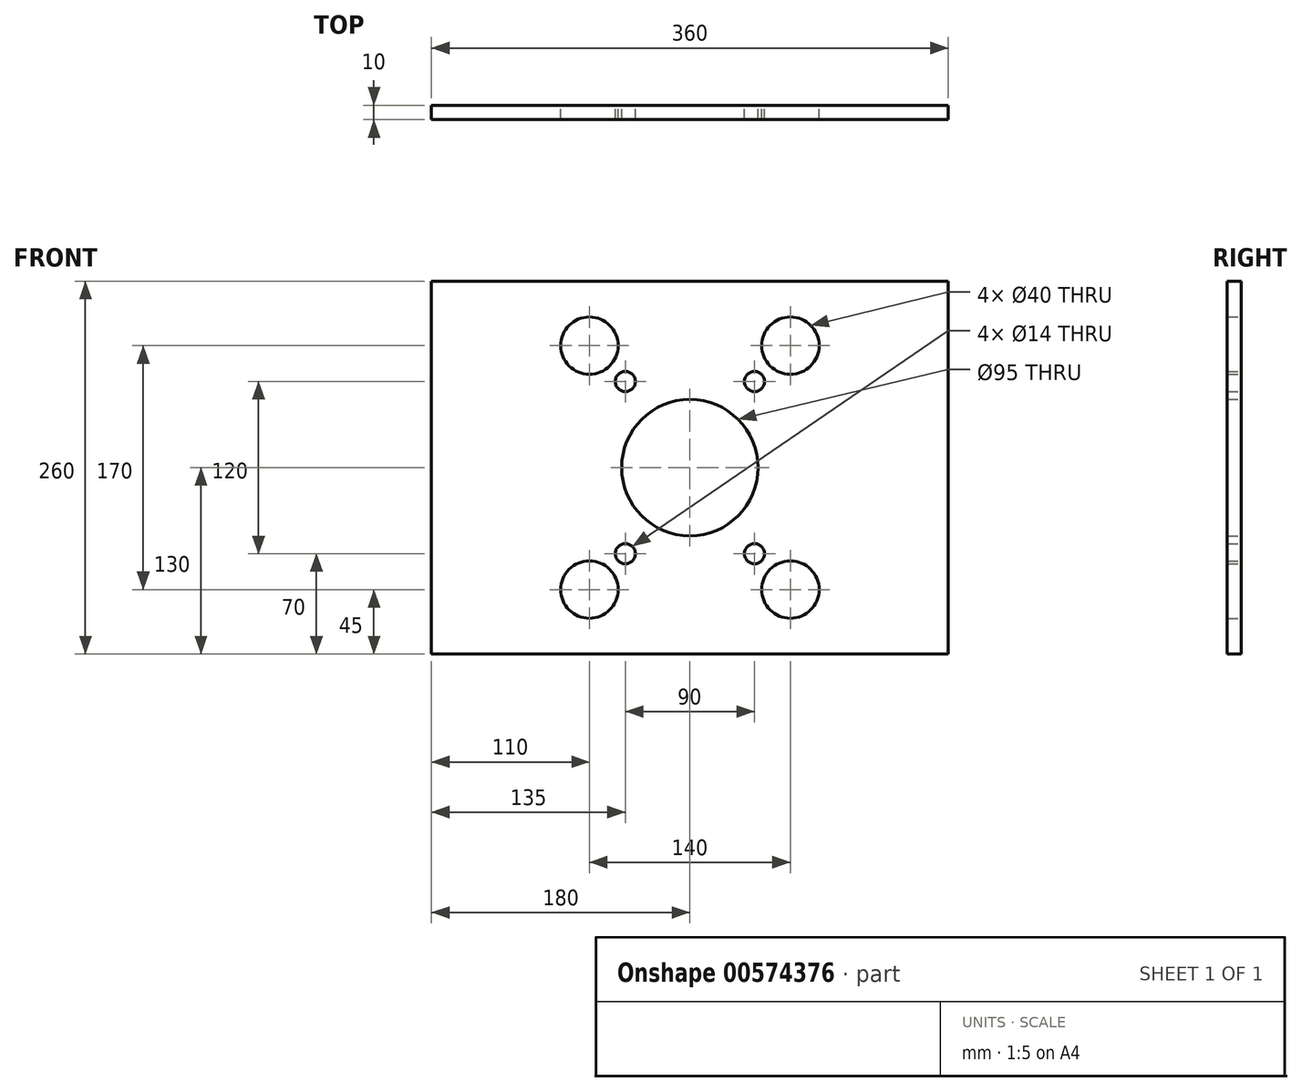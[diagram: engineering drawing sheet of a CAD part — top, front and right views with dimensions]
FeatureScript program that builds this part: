
annotation { "Feature Type Name" : "Feature", "Feature Type Description" : "" }
export const myFeature = defineFeature(function(context is Context, id is Id, definition is map)
    precondition{}
    {
        {
            var Q0;
            Q0=qCreatedBy(makeId("Front.planeOp"),FACE);
            var sketch = newSketch(context, id + "F0", { "sketchPlane" : qUnion([Q0])});
            skLineSegment(sketch, "E0.bottom", {"start": v(-180, 130) * mm, "end": v(180, 130) * mm});
            skLineSegment(sketch, "E0.top", {"start": v(-180, -130) * mm, "end": v(180, -130) * mm});
            skLineSegment(sketch, "E0.left", {"start": v(-180, 130) * mm, "end": v(-180, -130) * mm});
            skLineSegment(sketch, "E0.right", {"start": v(180, 130) * mm, "end": v(180, -130) * mm});
            skLineSegment(sketch, "E1", {"start": v(-180, 85) * mm, "end": v(180, 85) * mm, "construction": true});
            skLineSegment(sketch, "E2", {"start": v(-180, -85) * mm, "end": v(180, -85) * mm, "construction": true});
            skCircle(sketch, "E3", {"center": v(-70, 85) * mm, "radius": 20 * mm});
            skCircle(sketch, "E4", {"center": v(70, 85) * mm, "radius": 20 * mm});
            skCircle(sketch, "E5", {"center": v(-70, -85) * mm, "radius": 20 * mm});
            skCircle(sketch, "E6", {"center": v(70, -85) * mm, "radius": 20 * mm});
            skLineSegment(sketch, "E7", {"start": v(-180, 60) * mm, "end": v(180, 60) * mm, "construction": true});
            skLineSegment(sketch, "E8", {"start": v(-180, -60) * mm, "end": v(180, -60) * mm, "construction": true});
            skCircle(sketch, "E9", {"center": v(0, 0) * mm, "radius": 47.5 * mm});
            skCircle(sketch, "E10", {"center": v(-45, 60) * mm, "radius": 7 * mm});
            skCircle(sketch, "E11", {"center": v(-45, -60) * mm, "radius": 7 * mm});
            skCircle(sketch, "E12", {"center": v(45, 60) * mm, "radius": 7 * mm});
            skCircle(sketch, "E13", {"center": v(45, -60) * mm, "radius": 7 * mm});
            skSolve(sketch);
        }
        {
            var Q0;
            Q0=makeQuery(id+"F0.imprint","IMPRINT",FACE,{"disambiguationData":[TD([[makeQuery(id+"F0.imprint","IMPRINT",EDGE,{"derivedFrom":sQuery(id+"F0.wireOp",EDGE,"E0.bottom")}),-1.0]])]});
            extrude(context, id + "F1", {"entities" : qUnion([Q0]), "depth" : 10 * mm, "offsetDistance" : 25 * mm});
        }
    });
